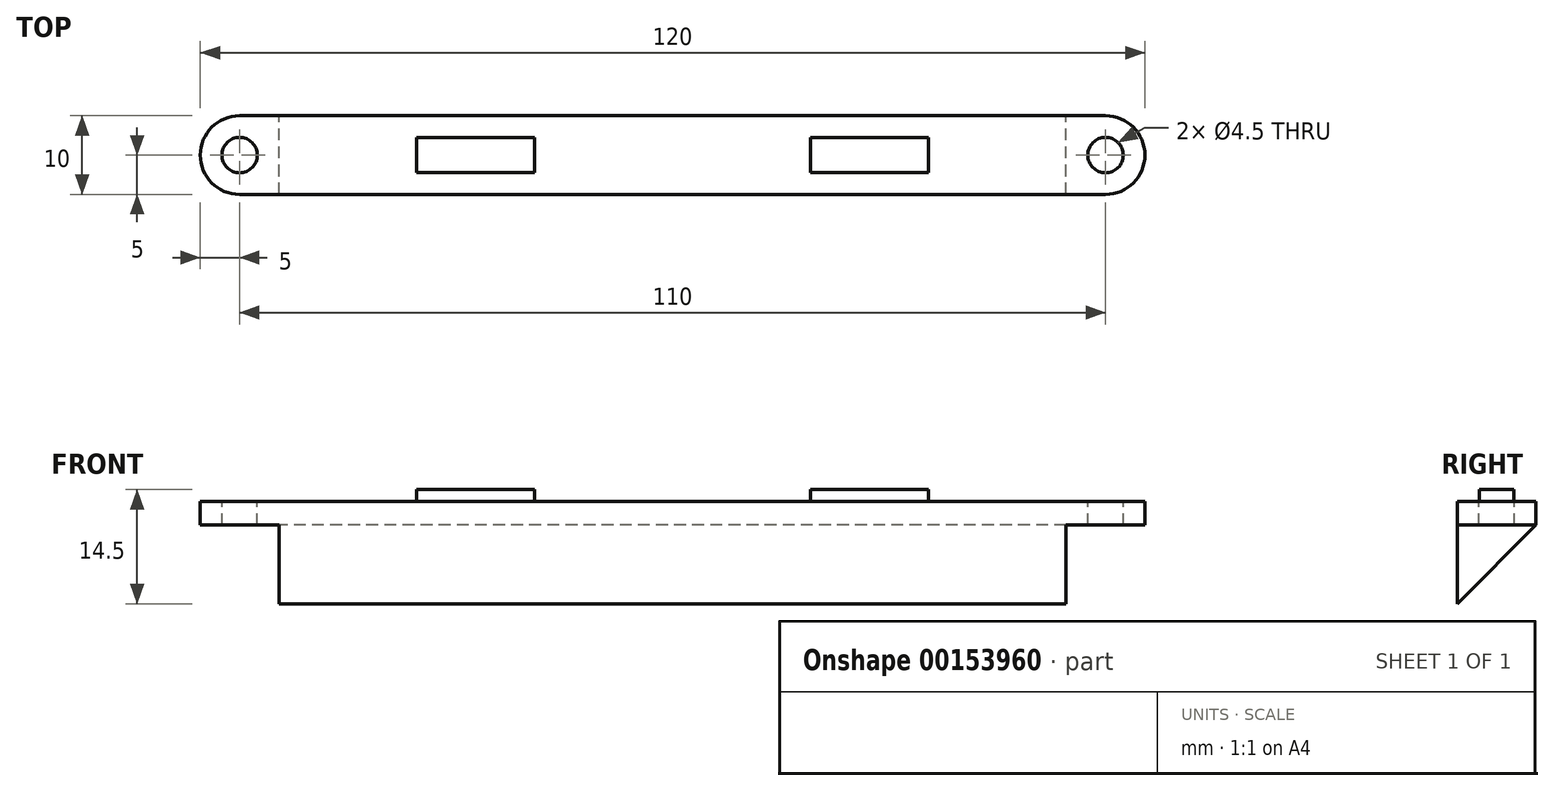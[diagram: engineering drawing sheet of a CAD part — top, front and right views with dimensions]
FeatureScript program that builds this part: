
annotation { "Feature Type Name" : "Feature", "Feature Type Description" : "" }
export const myFeature = defineFeature(function(context is Context, id is Id, definition is map)
    precondition{}
    {
        {
            var Q0;
            Q0=qCreatedBy(makeId("Top.planeOp"),FACE);
            var sketch = newSketch(context, id + "F0", { "sketchPlane" : qUnion([Q0])});
            skCircle(sketch, "E0", {"center": v(55, 0) * mm, "radius": 5 * mm});
            skCircle(sketch, "E1", {"center": v(-55, 0) * mm, "radius": 5 * mm});
            skLineSegment(sketch, "E2.bottom", {"start": v(-17.5, 2.2) * mm, "end": v(-32.5, 2.2) * mm});
            skLineSegment(sketch, "E2.top", {"start": v(-17.5, -2.2) * mm, "end": v(-32.5, -2.2) * mm});
            skLineSegment(sketch, "E2.left", {"start": v(-17.5, 2.2) * mm, "end": v(-17.5, -2.2) * mm});
            skLineSegment(sketch, "E2.right", {"start": v(-32.5, 2.2) * mm, "end": v(-32.5, -2.2) * mm});
            skPoint(sketch, "E2.middle", {"position": v(-25, 0) * mm});
            skLineSegment(sketch, "E3.bottom", {"start": v(32.5, 2.2) * mm, "end": v(17.5, 2.2) * mm});
            skLineSegment(sketch, "E3.top", {"start": v(32.5, -2.2) * mm, "end": v(17.5, -2.2) * mm});
            skLineSegment(sketch, "E3.left", {"start": v(32.5, 2.2) * mm, "end": v(32.5, -2.2) * mm});
            skLineSegment(sketch, "E3.right", {"start": v(17.5, 2.2) * mm, "end": v(17.5, -2.2) * mm});
            skPoint(sketch, "E3.middle", {"position": v(25, 0) * mm});
            skCircle(sketch, "E4", {"center": v(-55, 0) * mm, "radius": 2.25 * mm});
            skCircle(sketch, "E5", {"center": v(55, 0) * mm, "radius": 2.25 * mm});
            skLineSegment(sketch, "E6", {"start": v(-55, 5) * mm, "end": v(55, 5) * mm});
            skLineSegment(sketch, "E7", {"start": v(55, -5) * mm, "end": v(-55, -5) * mm});
            skSolve(sketch);
        }
        {
            var Q0;
            Q0=makeQuery(id+"F0.imprint","IMPRINT",FACE,{"disambiguationData":[TD([[makeQuery(id+"F0.imprint","IMPRINT",EDGE,{"derivedFrom":sQuery(id+"F0.wireOp",EDGE,"E4")}),-1.0]])]});
            var Q1;
            Q1=makeQuery(id+"F0.imprint","IMPRINT",FACE,{"disambiguationData":[TD([[makeQuery(id+"F0.imprint","IMPRINT",EDGE,{"derivedFrom":sQuery(id+"F0.wireOp",EDGE,"E2.bottom")}),-1.0]])]});
            var Q2;
            Q2=makeQuery(id+"F0.imprint","IMPRINT",FACE,{"disambiguationData":[TD([[makeQuery(id+"F0.imprint","IMPRINT",EDGE,{"derivedFrom":sQuery(id+"F0.wireOp",EDGE,"E2.bottom")}),1.0]])]});
            var Q3;
            Q3=makeQuery(id+"F0.imprint","IMPRINT",FACE,{"disambiguationData":[TD([[makeQuery(id+"F0.imprint","IMPRINT",EDGE,{"derivedFrom":sQuery(id+"F0.wireOp",EDGE,"E3.bottom")}),1.0]])]});
            var Q4;
            Q4=makeQuery(id+"F0.imprint","IMPRINT",FACE,{"disambiguationData":[TD([[makeQuery(id+"F0.imprint","IMPRINT",EDGE,{"derivedFrom":sQuery(id+"F0.wireOp",EDGE,"E5")}),-1.0]])]});
            extrude(context, id + "F1", {"entities" : qUnion([Q0, Q1, Q2, Q3, Q4]), "oppositeDirection" : true, "depth" : 3 * mm});
        }
        {
            var Q0;
            Q0=makeQuery(id+"F0.imprint","IMPRINT",FACE,{"disambiguationData":[TD([[makeQuery(id+"F0.imprint","IMPRINT",EDGE,{"derivedFrom":sQuery(id+"F0.wireOp",EDGE,"E2.bottom")}),1.0]])]});
            var Q1;
            Q1=makeQuery(id+"F0.imprint","IMPRINT",FACE,{"disambiguationData":[TD([[makeQuery(id+"F0.imprint","IMPRINT",EDGE,{"derivedFrom":sQuery(id+"F0.wireOp",EDGE,"E3.bottom")}),1.0]])]});
            extrude(context, id + "F2", {"entities" : qUnion([Q0, Q1]), "operationType" : NewBodyOperationType.ADD, "depth" : 1.5 * mm});
        }
        {
            var Q0;
            Q0=qCreatedBy(makeId("Right.planeOp"),FACE);
            var sketch = newSketch(context, id + "F3", { "sketchPlane" : qUnion([Q0])});
            skLineSegment(sketch, "E8", {"start": v(-5, -3) * mm, "end": v(5, -3) * mm});
            skLineSegment(sketch, "E9", {"start": v(5, -3) * mm, "end": v(-5, -13) * mm});
            skLineSegment(sketch, "E10", {"start": v(-5, -13) * mm, "end": v(-5, -3) * mm});
            skSolve(sketch);
        }
        {
            var Q0;
            Q0=makeQuery(id+"F3.imprint","IMPRINT",FACE,{"disambiguationData":[TD([[makeQuery(id+"F3.imprint","IMPRINT",EDGE,{"derivedFrom":sQuery(id+"F3.wireOp",EDGE,"E8")}),-1.0]])]});
            extrude(context, id + "F4", {"entities" : qUnion([Q0]), "operationType" : NewBodyOperationType.ADD, "endBound" : BoundingType.SYMMETRIC, "depth" : 100 * mm});
        }
    });
